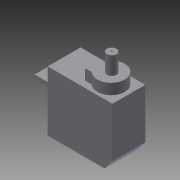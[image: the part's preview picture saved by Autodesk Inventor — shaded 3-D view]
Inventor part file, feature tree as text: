
AUTODESK INVENTOR PART (.ipt)
format: ipt  version: 2015 (Build 190159000, 159)  size: 164,864 bytes
history: native  units: in
note: dims shown in document units (in); Inventor stores cm internally (conversion verified against a paired STEP export)
features: extrude x10, sketch x10, projected_geometry x2
ambient origin geometry x8: Origin, YZ Plane, XZ Plane, XY Plane, X Axis, Y Axis, Z Axis, Center Point
bodies: Solid1 (feature_tree)
feature tree (22):
  extrude  "Extrusion1"  Depth=0.91in
  extrude  "Extrusion2"  Depth=0.462in TaperAngle=0.0deg
  extrude  "Extrusion3"  Depth=0.06in
  extrude  "Extrusion4"  Depth=0.19in
  extrude  "Extrusion5"  Depth=0.3855in
  extrude  "Extrusion6"  Depth=0.15in TaperAngle=0.0deg
  extrude  "Extrusion7"  Depth=0.25in TaperAngle=0.0deg
  extrude  "Extrusion8"  Depth=0.1828in
  extrude  "Extrusion9"  Depth=0.12in
  extrude  "Extrusion10"  Depth=0.462in
  sketch  "Sketch1"  dims[d0=0.592in d1=0.91in]
  sketch  "Sketch2"  dims[d2=0.462in d3=0.0in d4=0.462in d5=0.0in]
  sketch  "Sketch3"  dims[d6=1.25in d7=0.06in]
  sketch  "Sketch4"  dims[d8=0.462in d9=0.0in d10=0.19in]
  sketch  "Sketch5"  dims[d11=0.5in d12=0.0in d14=0.3855in]
  sketch  "Sketch6"  dims[d15=0.15in d16=0.0in d17=0.157in d18=0.0in]
  sketch  "Sketch7"  dims[d19=0.135in d20=0.25in d21=0.0in]
  sketch  "Sketch8"  dims[d22=0.01in d23=0.0in d24=0.1828in]
  sketch  "Sketch9"  dims[d25=0.1571in d26=0.12in]
  projected_geometry  "Projected Loop1"
  sketch  "Sketch11"  dims[d27=0.0915in d28=0.462in d29=0.231in d30=0.12in d31=0.231in d32=0.0785in d33=1.0in d34=0.0in d35=0.0962in d36=0.1404in d37=0.04in d38=0.0367in d39=0.462in d40=0.231in d46=0.66in d47=1.0in d48=0.0in]
  projected_geometry  "Projected Loop5"
